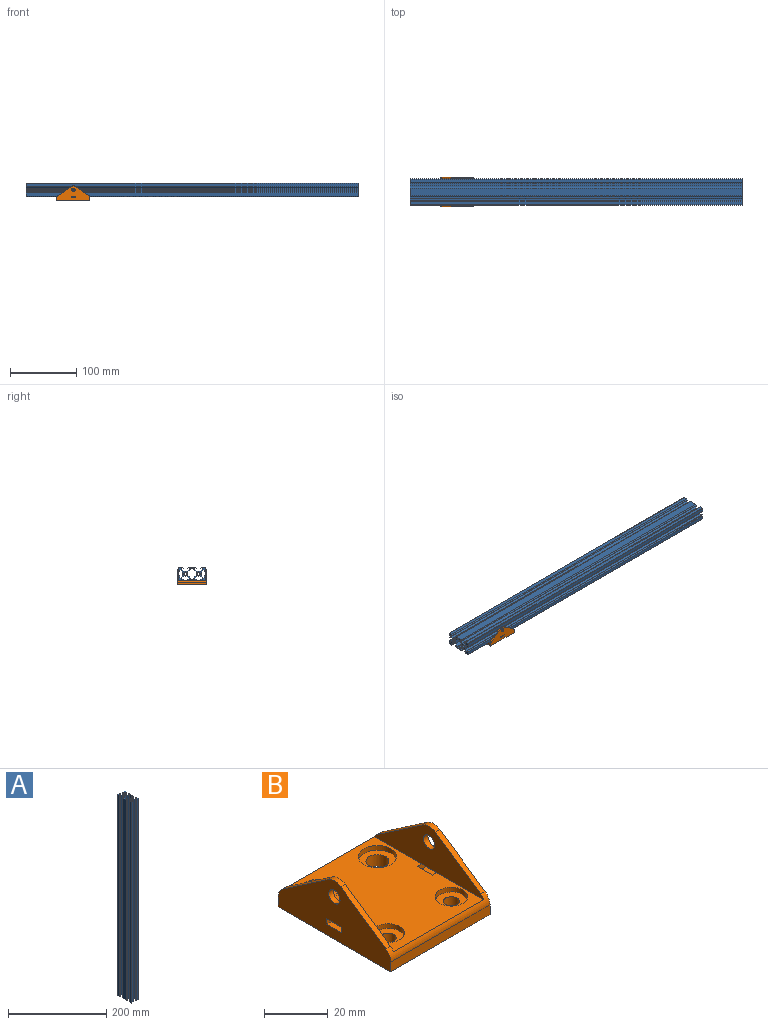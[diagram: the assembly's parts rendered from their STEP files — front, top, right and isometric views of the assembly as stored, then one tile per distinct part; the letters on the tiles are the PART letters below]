
ASSEMBLY  parts=2 mates=2
PART A: 114 faces, bbox 20x40x500 mm
  f0: cylinder r=2.1mm len=500mm, axis (0,0,-1), area 6597.3mm2, adj f112,f113
  f1: cylinder r=2.1mm len=500mm, axis (0,0,-1), area 6597.3mm2, adj f112,f113
  f2: plane 500x0.21mm, normal (0.71,0.71,0), area 148.5mm2, adj f3,f110,f112,f113
  f3: plane 500x0.21mm, normal (0.71,-0.71,0), area 148.5mm2, adj f2,f4,f112,f113
  f4: plane 500x2.63mm, normal (1,0,0), area 1314.7mm2, adj f3,f5,f112,f113
  f5: plane 500x2.66mm, normal (0.71,-0.71,0), area 1881.4mm2, adj f4,f6,f112,f113
  f6: plane 500x1.64mm, normal (0,-1,0), area 819.7mm2, adj f5,f7,f112,f113
  f7: plane 500x2.38mm, normal (-1,0,0), area 1187.5mm2, adj f6,f8,f112,f113
  f8: plane 500x0.35mm, normal (0,-1,0), area 172.5mm2, adj f7,f9,f112,f113
  f9: plane 500x1.46mm, normal (0.71,-0.71,0), area 1028.8mm2, adj f8,f10,f112,f113
  f10: plane 500x4.92mm, normal (1,0,0), area 2460mm2, adj f9,f11,f112,f113
  f11: cylinder r=0.5mm len=500mm, axis (0,0,-1), area 392.7mm2, adj f10,f12,f112,f113
  f12: plane 500x4.92mm, normal (0,1,0), area 2460mm2, adj f11,f13,f112,f113
  f13: plane 500x1.46mm, normal (-0.71,0.71,0), area 1028.8mm2, adj f12,f14,f112,f113
  f14: plane 500x0.35mm, normal (-1,0,0), area 172.5mm2, adj f13,f15,f112,f113
  f15: plane 500x2.38mm, normal (0,-1,0), area 1187.5mm2, adj f14,f16,f112,f113
  f16: plane 500x1.64mm, normal (-1,0,0), area 819.7mm2, adj f15,f17,f112,f113
  f17: plane 500x2.66mm, normal (-0.71,0.71,0), area 1881.4mm2, adj f16,f18,f112,f113
  f18: plane 500x2.63mm, normal (0,1,0), area 1314.7mm2, adj f17,f19,f112,f113
  f19: plane 500x0.21mm, normal (-0.71,0.71,0), area 148.5mm2, adj f18,f20,f112,f113
  f20: plane 500x0.21mm, normal (0.71,0.71,0), area 148.5mm2, adj f19,f21,f112,f113
  f21: plane 500x2.63mm, normal (0,1,0), area 1314.7mm2, adj f20,f22,f112,f113
  f22: plane 500x2.66mm, normal (0.71,0.71,0), area 1881.4mm2, adj f21,f23,f112,f113
  f23: plane 500x1.64mm, normal (1,0,0), area 819.7mm2, adj f22,f24,f112,f113
  f24: plane 500x2.38mm, normal (0,-1,0), area 1187.5mm2, adj f23,f25,f112,f113
  f25: plane 500x0.35mm, normal (1,0,0), area 172.5mm2, adj f24,f26,f112,f113
  f26: plane 500x1.46mm, normal (0.71,0.71,0), area 1028.8mm2, adj f25,f27,f112,f113
  f27: plane 500x4.92mm, normal (0,1,0), area 2460mm2, adj f26,f28,f112,f113
  f28: cylinder r=0.5mm len=500mm, axis (0,0,-1), area 392.7mm2, adj f27,f29,f112,f113
  f29: plane 500x4.92mm, normal (-1,0,0), area 2460mm2, adj f28,f30,f112,f113
  f30: plane 500x1.46mm, normal (-0.71,-0.71,0), area 1028.8mm2, adj f29,f31,f112,f113
  f31: plane 500x0.35mm, normal (0,-1,0), area 172.5mm2, adj f30,f32,f112,f113
  f32: plane 500x2.38mm, normal (1,0,0), area 1187.5mm2, adj f31,f33,f112,f113
  f33: plane 500x1.64mm, normal (0,-1,0), area 819.7mm2, adj f32,f34,f112,f113
  f34: plane 500x2.66mm, normal (-0.71,-0.71,0), area 1881.4mm2, adj f33,f35,f112,f113
  f35: plane 500x2.63mm, normal (-1,0,0), area 1314.7mm2, adj f34,f36,f112,f113
  f36: plane 500x0.21mm, normal (-0.71,-0.71,0), area 148.5mm2, adj f35,f37,f112,f113
  f37: plane 500x0.21mm, normal (-0.71,0.71,0), area 148.5mm2, adj f36,f38,f112,f113
  f38: plane 500x2.63mm, normal (-1,0,0), area 1314.7mm2, adj f37,f39,f112,f113
  f39: plane 500x2.66mm, normal (-0.71,0.71,0), area 1881.4mm2, adj f38,f40,f112,f113
  f40: plane 500x1.64mm, normal (0,1,0), area 819.7mm2, adj f39,f41,f112,f113
  f41: plane 500x2.38mm, normal (1,0,0), area 1187.5mm2, adj f40,f42,f112,f113
  f42: plane 500x0.35mm, normal (0,1,0), area 172.5mm2, adj f41,f43,f112,f113
  f43: plane 500x1.46mm, normal (-0.71,0.71,0), area 1028.8mm2, adj f42,f44,f112,f113
  f44: plane 500x10.84mm, normal (-1,0,0), area 5420mm2, adj f43,f45,f112,f113
  f45: plane 500x1.46mm, normal (-0.71,-0.71,0), area 1028.8mm2, adj f44,f46,f112,f113
  f46: plane 500x0.35mm, normal (0,-1,0), area 172.5mm2, adj f45,f47,f112,f113
  f47: plane 500x2.38mm, normal (1,0,0), area 1187.5mm2, adj f46,f48,f112,f113
  f48: plane 500x1.64mm, normal (0,-1,0), area 819.7mm2, adj f47,f49,f112,f113
  f49: plane 500x2.66mm, normal (-0.71,-0.71,0), area 1881.4mm2, adj f48,f50,f112,f113
  f50: plane 500x2.63mm, normal (-1,0,0), area 1314.7mm2, adj f49,f51,f112,f113
  f51: plane 500x0.21mm, normal (-0.71,-0.71,0), area 148.5mm2, adj f50,f52,f112,f113
  f52: plane 500x0.21mm, normal (-0.71,0.71,0), area 148.5mm2, adj f51,f53,f112,f113
  f53: plane 500x2.63mm, normal (-1,0,0), area 1314.7mm2, adj f52,f54,f112,f113
  f54: plane 500x2.66mm, normal (-0.71,0.71,0), area 1881.4mm2, adj f53,f55,f112,f113
  f55: plane 500x1.64mm, normal (0,1,0), area 819.7mm2, adj f54,f56,f112,f113
  f56: plane 500x2.38mm, normal (1,0,0), area 1187.5mm2, adj f55,f57,f112,f113
  f57: plane 500x0.35mm, normal (0,1,0), area 172.5mm2, adj f56,f58,f112,f113
  f58: plane 500x1.46mm, normal (-0.71,0.71,0), area 1028.8mm2, adj f57,f59,f112,f113
  f59: plane 500x4.92mm, normal (-1,0,0), area 2460mm2, adj f58,f60,f112,f113
  f60: cylinder r=0.5mm len=500mm, axis (0,0,-1), area 392.7mm2, adj f59,f61,f112,f113
  f61: plane 500x4.92mm, normal (0,-1,0), area 2460mm2, adj f60,f62,f112,f113
  f62: plane 500x1.46mm, normal (0.71,-0.71,0), area 1028.8mm2, adj f61,f63,f112,f113
  f63: plane 500x0.35mm, normal (1,0,0), area 172.5mm2, adj f62,f64,f112,f113
  f64: plane 500x2.38mm, normal (0,1,0), area 1187.5mm2, adj f63,f65,f112,f113
  f65: plane 500x1.64mm, normal (1,0,0), area 819.7mm2, adj f64,f66,f112,f113
  f66: plane 500x2.66mm, normal (0.71,-0.71,0), area 1881.4mm2, adj f65,f67,f112,f113
  f67: plane 500x2.63mm, normal (0,-1,0), area 1314.7mm2, adj f66,f68,f112,f113
  f68: plane 500x0.21mm, normal (0.71,-0.71,0), area 148.5mm2, adj f67,f69,f112,f113
  f69: plane 500x0.21mm, normal (-0.71,-0.71,0), area 148.5mm2, adj f68,f70,f112,f113
  f70: plane 500x2.63mm, normal (0,-1,0), area 1314.7mm2, adj f69,f71,f112,f113
  f71: plane 500x2.66mm, normal (-0.71,-0.71,0), area 1881.4mm2, adj f70,f72,f112,f113
  f72: plane 500x1.64mm, normal (-1,0,0), area 819.7mm2, adj f71,f73,f112,f113
  f73: plane 500x2.38mm, normal (0,1,0), area 1187.5mm2, adj f72,f74,f112,f113
  f74: plane 500x0.35mm, normal (-1,0,0), area 172.5mm2, adj f73,f75,f112,f113
  f75: plane 500x1.46mm, normal (-0.71,-0.71,0), area 1028.8mm2, adj f74,f76,f112,f113
  f76: plane 500x4.92mm, normal (0,-1,0), area 2460mm2, adj f75,f77,f112,f113
  f77: cylinder r=0.5mm len=500mm, axis (0,0,-1), area 392.7mm2, adj f76,f78,f112,f113
  f78: plane 500x4.92mm, normal (1,0,0), area 2460mm2, adj f77,f79,f112,f113
  f79: plane 500x1.46mm, normal (0.71,0.71,0), area 1028.8mm2, adj f78,f80,f112,f113
  f80: plane 500x0.35mm, normal (0,1,0), area 172.5mm2, adj f79,f81,f112,f113
  f81: plane 500x2.38mm, normal (-1,0,0), area 1187.5mm2, adj f80,f82,f112,f113
  f82: plane 500x1.64mm, normal (0,1,0), area 819.7mm2, adj f81,f83,f112,f113
  f83: plane 500x2.66mm, normal (0.71,0.71,0), area 1881.4mm2, adj f82,f84,f112,f113
  f84: plane 500x2.63mm, normal (1,0,0), area 1314.7mm2, adj f83,f85,f112,f113
  f85: plane 500x0.21mm, normal (0.71,0.71,0), area 148.5mm2, adj f84,f86,f112,f113
  f86: plane 500x0.21mm, normal (0.71,-0.71,0), area 148.5mm2, adj f85,f87,f112,f113
  f87: plane 500x2.63mm, normal (1,0,0), area 1314.7mm2, adj f86,f88,f112,f113
  f88: plane 500x2.66mm, normal (0.71,-0.71,0), area 1881.4mm2, adj f87,f89,f112,f113
  f89: plane 500x1.64mm, normal (0,-1,0), area 819.7mm2, adj f88,f90,f112,f113
  f90: plane 500x2.38mm, normal (-1,0,0), area 1187.5mm2, adj f89,f91,f112,f113
  f91: plane 500x0.35mm, normal (0,-1,0), area 172.5mm2, adj f90,f92,f112,f113
  f92: plane 500x1.46mm, normal (0.71,-0.71,0), area 1028.8mm2, adj f91,f93,f112,f113
  f93: plane 500x10.84mm, normal (1,0,0), area 5420mm2, adj f92,f94,f112,f113
  f94: plane 500x1.46mm, normal (0.71,0.71,0), area 1028.8mm2, adj f93,f95,f112,f113
  f95: plane 500x0.35mm, normal (0,1,0), area 172.5mm2, adj f94,f96,f112,f113
  f96: plane 500x2.38mm, normal (-1,0,0), area 1187.5mm2, adj f95,f97,f112,f113
  f97: plane 500x1.64mm, normal (0,1,0), area 819.7mm2, adj f96,f98,f112,f113
  f98: plane 500x2.66mm, normal (0.71,0.71,0), area 1881.4mm2, adj f97,f110,f112,f113
  f99: plane 500x1.96mm, normal (0,1,0), area 980.3mm2, adj f100,f111,f112,f113
  f100: plane 500x5.4mm, normal (1,0,0), area 2700mm2, adj f99,f101,f112,f113
  f101: plane 500x1.96mm, normal (0,-1,0), area 980.3mm2, adj f100,f102,f112,f113
  f102: plane 500x3.4mm, normal (0.71,-0.71,0), area 2404.2mm2, adj f101,f103,f112,f113
  f103: plane 500x5.68mm, normal (0,-1,0), area 2839.3mm2, adj f102,f104,f112,f113
  f104: plane 500x3.4mm, normal (-0.71,-0.71,0), area 2404.2mm2, adj f103,f105,f112,f113
  f105: plane 500x1.96mm, normal (0,-1,0), area 980.3mm2, adj f104,f106,f112,f113
  f106: plane 500x5.4mm, normal (-1,0,0), area 2700mm2, adj f105,f107,f112,f113
  f107: plane 500x1.96mm, normal (0,1,0), area 980.3mm2, adj f106,f108,f112,f113
  f108: plane 500x3.4mm, normal (-0.71,0.71,0), area 2404.2mm2, adj f107,f109,f112,f113
  f109: plane 500x5.68mm, normal (0,1,0), area 2839.3mm2, adj f108,f111,f112,f113
  f110: plane 500x2.63mm, normal (1,0,0), area 1314.7mm2, adj f2,f98,f112,f113
  f111: plane 500x3.4mm, normal (0.71,0.71,0), area 2404.2mm2, adj f99,f109,f112,f113
  f112: plane 40x20mm, normal (0,0,1), area 300mm2, adj f0,f1,f2,f3,f4,f5,f6,f7
  f113: plane 40x20mm, normal (0,0,-1), area 300mm2, adj f0,f1,f2,f3,f4,f5,f6,f7
PART B: 42 faces, bbox 44x50x22.4 mm
  f0: plane 6.7x4.17mm, normal (1,0,0), area 27.9mm2, adj f7,f17,f18,f19
  f1: plane 50x22.44mm, normal (-1,0,0), area 707.9mm2, adj f4,f5,f7,f12,f13,f14,f17,f18
  f2: cylinder r=3.6mm len=7.2mm, axis (0,0,1), area 102.9mm2, adj f7,f11
  f3: cylinder r=2.5mm len=5mm, axis (0,0,1), area 71.5mm2, adj f7,f9
  f4: plane 44x3.72mm, normal (0,1,0), area 163.5mm2, adj f1,f7,f23,f25
  f5: plane 44x3.72mm, normal (0,-1,0), area 163.5mm2, adj f1,f7,f21,f25
  f6: plane 48.5x40mm, normal (0,0,1), area 1523.6mm2, adj f8,f10,f15,f16,f17,f18,f21,f23
  f7: plane 50x44mm, normal (0,0,-1), area 2052.5mm2, adj f0,f1,f2,f3,f4,f5,f16,f17
  f8: cylinder r=5.1mm len=10.2mm, axis (0,0,1), area 57.7mm2, adj f6,f9
  f9: plane 10.2x10.2mm, normal (0,0,1), area 62.1mm2, adj f3,f8
  f10: cylinder r=6mm len=12mm, axis (0,0,1), area 67.9mm2, adj f6,f11
  f11: plane 12x12mm, normal (0,0,1), area 72.4mm2, adj f2,f10
  f12: plane 20x13.72mm, normal (0,0.57,0.82), area 48.5mm2, adj f1,f15,f22,f23
  f13: plane 20x13.72mm, normal (0,-0.57,0.82), area 48.5mm2, adj f1,f15,f21,f22
  f14: cylinder r=2.5mm len=5mm, axis (-1,0,0), area 31.4mm2, adj f1,f15
  f15: plane 48.5x16.09mm, normal (1,0,0), area 406.2mm2, adj f6,f12,f13,f14,f20,f21,f22,f23
  f16: plane 6.7x6.35mm, normal (-1,0,0), area 42.5mm2, adj f6,f7,f17,f18
  f17: plane 6.35x4mm, normal (0,-1,0), area 17.1mm2, adj f0,f1,f6,f7,f16,f19,f20
  f18: plane 6.35x4mm, normal (0,1,0), area 17.1mm2, adj f0,f1,f6,f7,f16,f19,f20
  f19: plane 6.7x2mm, normal (0,0,1), area 13.4mm2, adj f0,f1,f17,f18
  f20: plane 6.7x2mm, normal (0,0,-1), area 13.4mm2, adj f1,f15,f17,f18
  f21: cylinder r=5mm len=44mm, axis (-1,0,0), area 130.3mm2, adj f1,f5,f6,f13,f15,f25,f33,f35
  f22: cylinder r=5mm len=5.66mm, axis (-1,0,0), area 12mm2, adj f1,f12,f13,f15
  f23: cylinder r=5mm len=44mm, axis (1,0,0), area 130.3mm2, adj f1,f4,f6,f12,f15,f25,f32,f35
  f24: plane 6.7x4.17mm, normal (-1,0,0), area 27.9mm2, adj f7,f37,f38,f39
  f25: plane 50x22.44mm, normal (1,0,0), area 707.9mm2, adj f4,f5,f7,f21,f23,f32,f33,f34
  f26: cylinder r=3.6mm len=7.2mm, axis (0,0,1), area 102.9mm2, adj f7,f31
  f27: cylinder r=2.5mm len=5mm, axis (0,0,1), area 71.5mm2, adj f7,f29
  f28: cylinder r=5.1mm len=10.2mm, axis (0,0,1), area 57.7mm2, adj f6,f29
  f29: plane 10.2x10.2mm, normal (0,0,1), area 62.1mm2, adj f27,f28
  f30: cylinder r=6mm len=12mm, axis (0,0,1), area 67.9mm2, adj f6,f31
  f31: plane 12x12mm, normal (0,0,1), area 72.4mm2, adj f26,f30
  f32: plane 20x13.72mm, normal (0,0.57,0.82), area 48.5mm2, adj f23,f25,f35,f41
  f33: plane 20x13.72mm, normal (0,-0.57,0.82), area 48.5mm2, adj f21,f25,f35,f41
  f34: cylinder r=2.5mm len=5mm, axis (1,0,0), area 31.4mm2, adj f25,f35
  f35: plane 48.5x16.09mm, normal (-1,0,0), area 406.2mm2, adj f6,f21,f23,f32,f33,f34,f40,f41
  f36: plane 6.7x6.35mm, normal (1,0,0), area 42.5mm2, adj f6,f7,f37,f38
  f37: plane 6.35x4mm, normal (0,-1,0), area 17.1mm2, adj f6,f7,f24,f25,f36,f39,f40
  f38: plane 6.35x4mm, normal (0,1,0), area 17.1mm2, adj f6,f7,f24,f25,f36,f39,f40
  f39: plane 6.7x2mm, normal (0,0,1), area 13.4mm2, adj f24,f25,f37,f38
  f40: plane 6.7x2mm, normal (0,0,-1), area 13.4mm2, adj f25,f35,f37,f38
  f41: cylinder r=5mm len=5.66mm, axis (1,0,0), area 12mm2, adj f25,f32,f33,f35
PLACE A rot(axis=(0.71,0,-0.71),180deg) t=(0.67,-66.4,-20.07)mm
PLACE B rot(axis=(0,0,1),90deg) t=(-426.02,-38.4,-36.42)mm
MATE planar A.f27 <-> B.f15  axis (0,-1,0) through (-249.33,-86.4,-13.03)mm
MATE planar B.f6 <-> A.f93  axis (0,0,1) through (-427.33,-66.4,-30.07)mm
